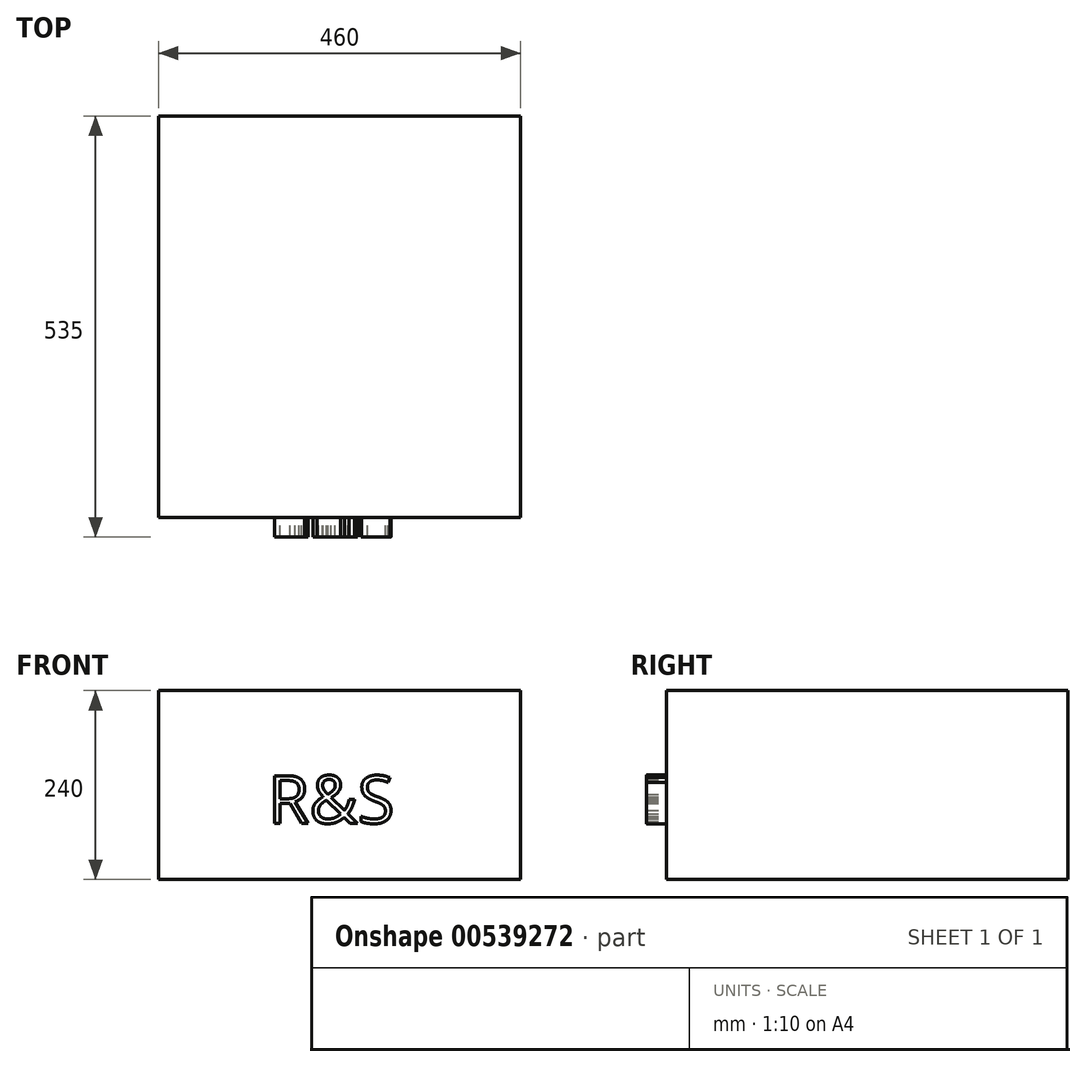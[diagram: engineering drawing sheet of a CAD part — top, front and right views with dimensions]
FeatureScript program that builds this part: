
annotation { "Feature Type Name" : "Feature", "Feature Type Description" : "" }
export const myFeature = defineFeature(function(context is Context, id is Id, definition is map)
    precondition{}
    {
        {
            var Q0;
            Q0=qCreatedBy(makeId("Front.planeOp"),FACE);
            var sketch = newSketch(context, id + "F0", { "sketchPlane" : qUnion([Q0])});
            skLineSegment(sketch, "E0.bottom", {"start": v(-230, -120) * mm, "end": v(230, -120) * mm});
            skLineSegment(sketch, "E0.top", {"start": v(-230, 120) * mm, "end": v(230, 120) * mm});
            skLineSegment(sketch, "E0.left", {"start": v(-230, -120) * mm, "end": v(-230, 120) * mm});
            skLineSegment(sketch, "E0.right", {"start": v(230, -120) * mm, "end": v(230, 120) * mm});
            skPoint(sketch, "E0.middle", {"position": v(0, 0) * mm});
            skSolve(sketch);
        }
        {
            var Q0;
            Q0 = qSketchRegion(id + "F0", true);
            var Q1;
            Q1=makeQuery(id+"F0.imprint","IMPRINT",FACE,{"disambiguationData":[TD([[makeQuery(id+"F0.imprint","IMPRINT",EDGE,{"derivedFrom":sQuery(id+"F0.wireOp",EDGE,"E0.bottom")}),1.0]])]});
            extrude(context, id + "F1", {"entities" : qUnion([Q0, Q1]), "endBound" : BoundingType.SYMMETRIC, "depth" : 510 * mm, "offsetDistance" : 25 * mm});
        }
        {
            var Q0;
            Q0=makeQuery(id+"F1.opExtrude","CAP_FACE",FACE,{"disambiguationData":[OSD([sQuery(id+"F0.wireOp",EDGE,"E0.bottom"),sQuery(id+"F0.wireOp",EDGE,"E0.top"),sQuery(id+"F0.wireOp",EDGE,"E0.left"),sQuery(id+"F0.wireOp",EDGE,"E0.right")])],"isStart":false});
            var sketch = newSketch(context, id + "F2", { "sketchPlane" : qUnion([Q0])});
            skText(sketch, "E1", { "text": "R&S", "fontName": "OpenSans-Regular.ttf"});
            const initialGuessF2  = {"E1": [-0.0908, -0.04838, 1, 0, 0.06077]};
            skSetInitialGuess(sketch, initialGuessF2);
            skSolve(sketch);
        }
        {
            var Q0;
            Q0 = qSketchRegion(id + "F2", true);
            extrude(context, id + "F3", {"entities" : qUnion([Q0]), "operationType" : NewBodyOperationType.ADD, "depth" : 25 * mm, "offsetDistance" : 25 * mm});
        }
    });
